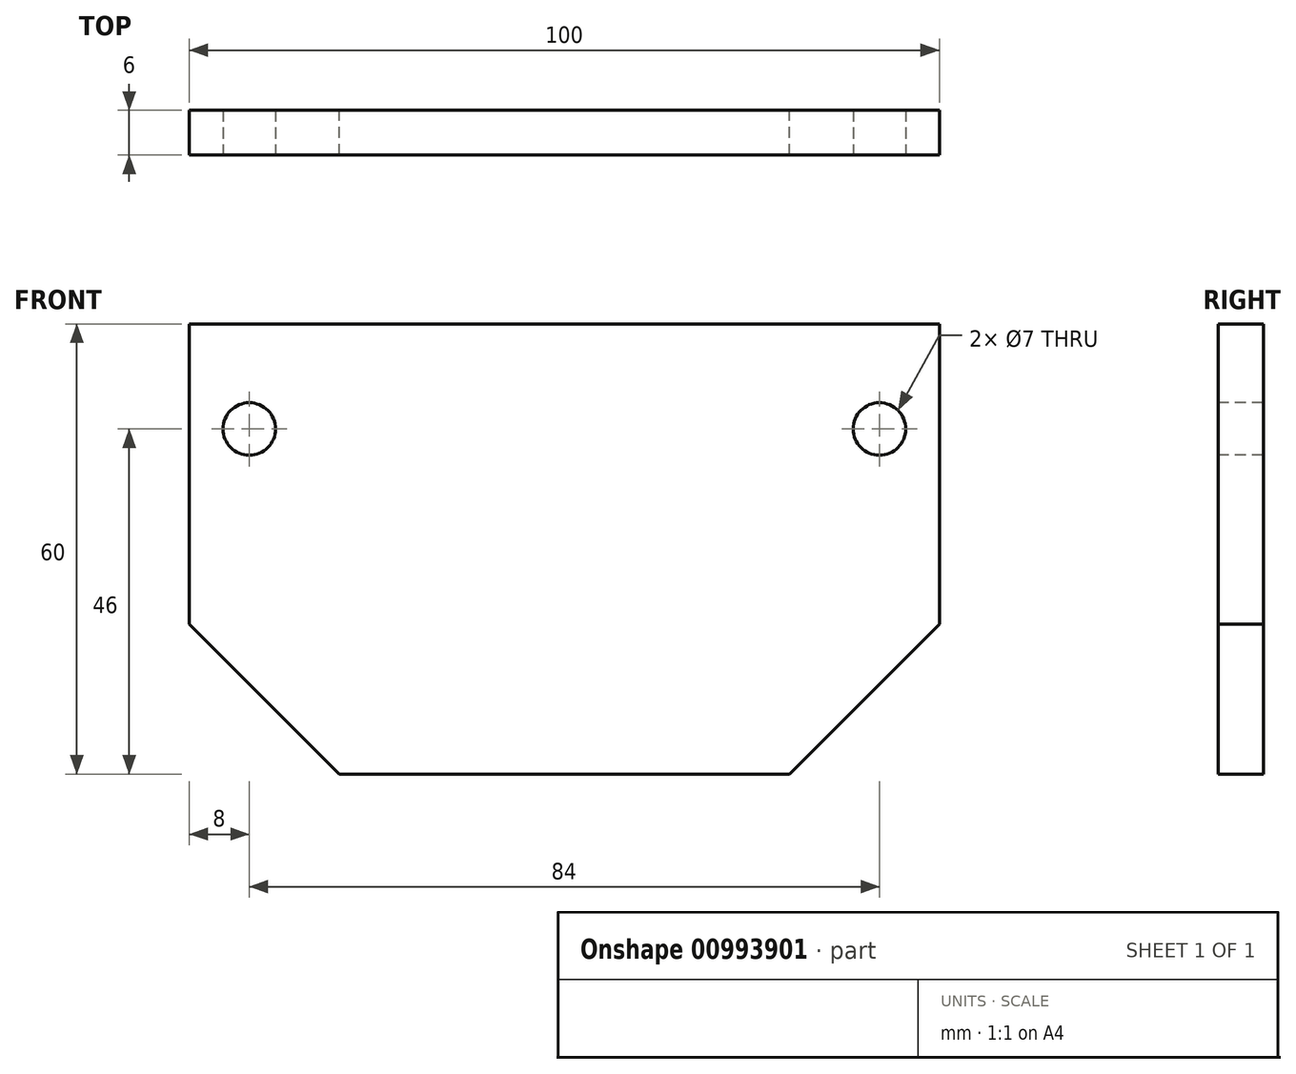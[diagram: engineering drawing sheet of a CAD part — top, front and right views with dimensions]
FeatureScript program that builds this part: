
annotation { "Feature Type Name" : "Feature", "Feature Type Description" : "" }
export const myFeature = defineFeature(function(context is Context, id is Id, definition is map)
    precondition{}
    {
        {
            var Q0;
            Q0=qCreatedBy(makeId("Front.planeOp"),FACE);
            var sketch = newSketch(context, id + "F0", { "sketchPlane" : qUnion([Q0])});
            skLineSegment(sketch, "E0.bottom", {"start": v(0, 0) * mm, "end": v(100, 0) * mm});
            skLineSegment(sketch, "E0.top", {"start": v(0, 40) * mm, "end": v(100, 40) * mm});
            skLineSegment(sketch, "E0.left", {"start": v(0, 0) * mm, "end": v(0, 40) * mm});
            skLineSegment(sketch, "E0.right", {"start": v(100, 0) * mm, "end": v(100, 40) * mm});
            skLineSegment(sketch, "E1", {"start": v(0, 0) * mm, "end": v(20, -20) * mm});
            skLineSegment(sketch, "E2", {"start": v(20, -20) * mm, "end": v(80, -20) * mm});
            skLineSegment(sketch, "E3", {"start": v(80, -20) * mm, "end": v(100, 0) * mm});
            skSolve(sketch);
        }
        {
            var Q0;
            Q0 = qSketchRegion(id + "F0", true);
            extrude(context, id + "F1", {"entities" : qUnion([Q0]), "depth" : 6 * mm, "offsetDistance" : 25 * mm});
        }
        {
            var Q0;
            Q0=makeQuery(id+"F1.opExtrude","CAP_FACE",FACE,{"disambiguationData":[OSD([sQuery(id+"F0.wireOp",EDGE,"E0.top"),sQuery(id+"F0.wireOp",EDGE,"E0.left"),sQuery(id+"F0.wireOp",EDGE,"E0.right"),sQuery(id+"F0.wireOp",EDGE,"E1"),sQuery(id+"F0.wireOp",EDGE,"E2"),sQuery(id+"F0.wireOp",EDGE,"E3")])],"isStart":false});
            var sketch = newSketch(context, id + "F2", { "sketchPlane" : qUnion([Q0])});
            skCircle(sketch, "E4", {"center": v(8, 26) * mm, "radius": 3.5 * mm});
            skCircle(sketch, "E5", {"center": v(92, 26) * mm, "radius": 3.5 * mm});
            skSolve(sketch);
        }
        {
            var Q0;
            Q0 = qSketchRegion(id + "F2", true);
            extrude(context, id + "F3", {"entities" : qUnion([Q0]), "operationType" : NewBodyOperationType.REMOVE, "endBound" : BoundingType.THROUGH_ALL, "oppositeDirection" : true, "depth" : 25 * mm, "offsetDistance" : 25 * mm});
        }
    });
